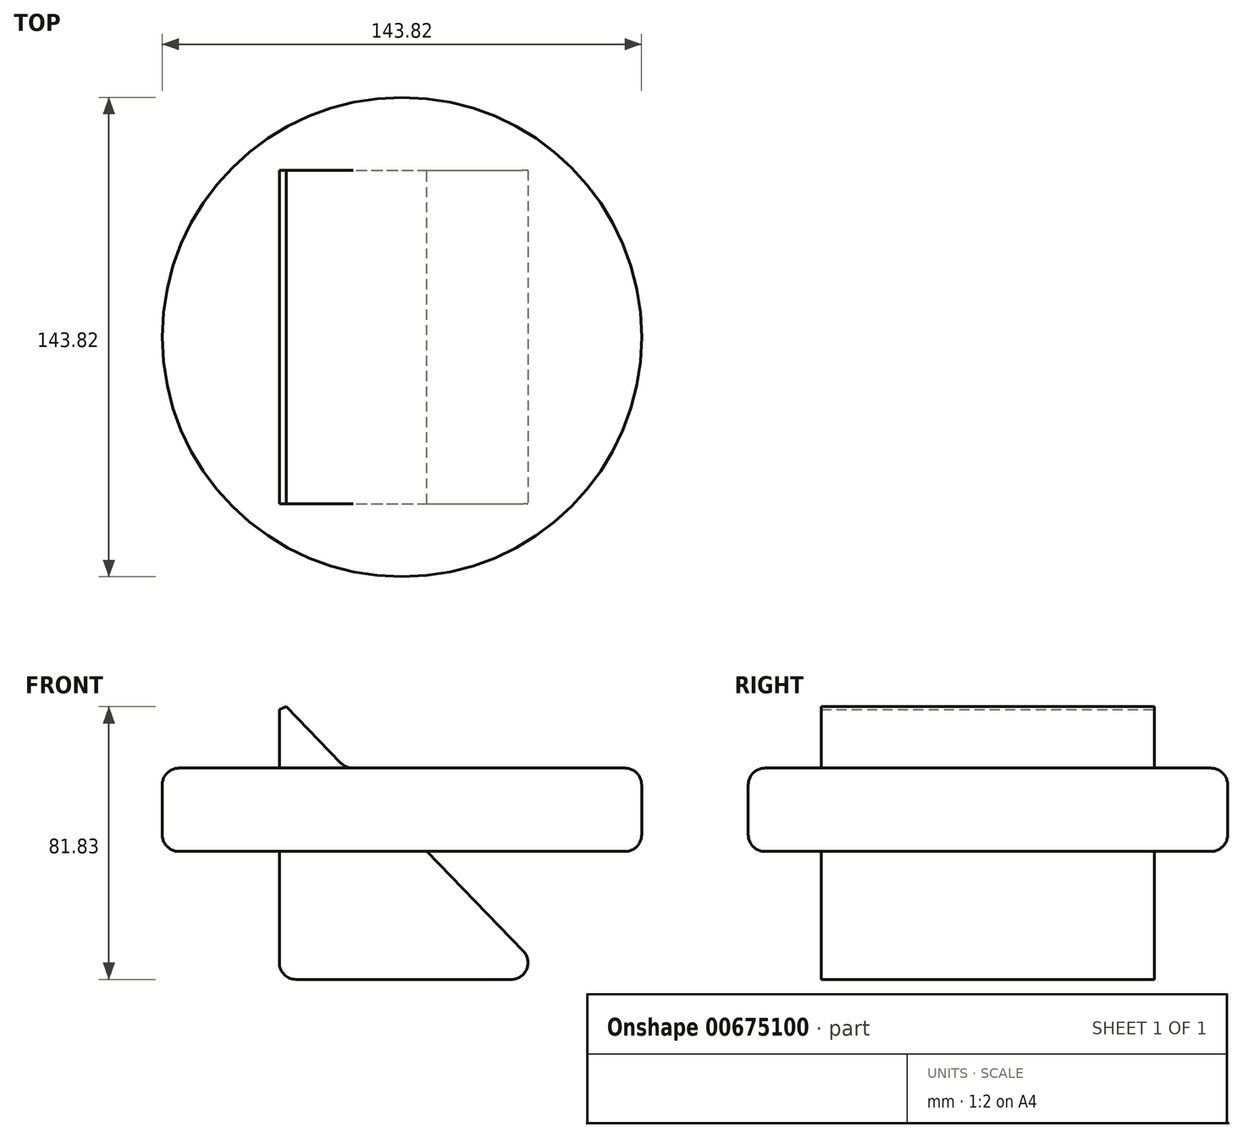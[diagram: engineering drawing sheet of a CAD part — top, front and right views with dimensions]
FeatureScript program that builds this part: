
annotation { "Feature Type Name" : "Feature", "Feature Type Description" : "" }
export const myFeature = defineFeature(function(context is Context, id is Id, definition is map)
    precondition{}
    {
        {
            var Q0;
            Q0=qCreatedBy(makeId("Top.planeOp"),FACE);
            var sketch = newSketch(context, id + "F0", { "sketchPlane" : qUnion([Q0])});
            skCircle(sketch, "E0", {"center": v(0, 0) * mm, "radius": 71.91 * mm});
            skSolve(sketch);
        }
        {
            var Q0;
            Q0=makeQuery(id+"F0.imprint","IMPRINT",FACE,{"disambiguationData":[TD([[makeQuery(id+"F0.imprint","IMPRINT",EDGE,{"derivedFrom":sQuery(id+"F0.wireOp",EDGE,"E0")}),1.0]])]});
            extrude(context, id + "F1", {"entities" : qUnion([Q0]), "depth" : 25 * mm, "offsetDistance" : 25 * mm});
        }
        {
            var Q0;
            Q0=qCreatedBy(makeId("Front.planeOp"),FACE);
            var sketch = newSketch(context, id + "F2", { "sketchPlane" : qUnion([Q0])});
            skLineSegment(sketch, "E1", {"start": v(-36.8, 42.55) * mm, "end": v(-36.8, -38.4) * mm});
            skLineSegment(sketch, "E2", {"start": v(-36.8, -38.4) * mm, "end": v(44.6, -38.4) * mm});
            skLineSegment(sketch, "E3", {"start": v(-34.66, 43.44) * mm, "end": v(44.6, -38.4) * mm});
            skLineSegment(sketch, "E4", {"start": v(-34.66, 43.44) * mm, "end": v(-36.8, 42.55) * mm});
            skSolve(sketch);
        }
        {
            var Q0;
            Q0 = qSketchRegion(id + "F2", true);
            extrude(context, id + "F3", {"entities" : qUnion([Q0]), "operationType" : NewBodyOperationType.ADD, "endBound" : BoundingType.SYMMETRIC, "depth" : 100 * mm, "offsetDistance" : 25 * mm});
        }
        {
            var Q0;
            Q0=makeQuery(id+"F3.opExtrude","SWEPT_EDGE",EDGE,{"disambiguationData":[OSD([sQuery(id+"F2.wireOp",EDGE,"E2"),sQuery(id+"F2.wireOp",EDGE,"E3")])]});
            fillet(context, id + "F4", {"entities" : qUnion([Q0]), "radius" : 5 * mm, "tangentPropagation" : true, "allowEdgeOverflow" : false});
        }
        {
            var Q0;
            Q0=makeQuery(id+"F3.opExtrude","SWEPT_EDGE",EDGE,{"disambiguationData":[OSD([sQuery(id+"F2.wireOp",EDGE,"E1"),sQuery(id+"F2.wireOp",EDGE,"E2")])]});
            fillet(context, id + "F5", {"entities" : qUnion([Q0]), "radius" : 5 * mm, "tangentPropagation" : true, "allowEdgeOverflow" : false});
        }
        {
            var Q0;
            Q0=makeQuery(id+"F1.opExtrude","CAP_EDGE",EDGE,{"disambiguationData":[OSD([sQuery(id+"F0.wireOp",EDGE,"E0")])],"isStart":false});
            fillet(context, id + "F6", {"entities" : qUnion([Q0]), "radius" : 5 * mm, "tangentPropagation" : true, "allowEdgeOverflow" : false});
        }
        {
            var Q0;
            Q0=makeQuery(id+"F1.opExtrude","CAP_EDGE",EDGE,{"disambiguationData":[OSD([sQuery(id+"F0.wireOp",EDGE,"E0")])],"isStart":true});
            fillet(context, id + "F7", {"entities" : qUnion([Q0]), "radius" : 5 * mm, "tangentPropagation" : true, "allowEdgeOverflow" : false});
        }
        {
            var Q0;
            Q0=makeQuery(id+"F3.boolean.opBoolean","INTERSECT",EDGE,{"derivedFrom":[makeQuery(id+"F1.opExtrude","CAP_FACE",FACE,{"disambiguationData":[OSD([sQuery(id+"F0.wireOp",EDGE,"E0")])],"isStart":false}),makeQuery(id+"F3.opExtrude","SWEPT_FACE",FACE,{"disambiguationData":[OSD([sQuery(id+"F2.wireOp",EDGE,"E3")])]})]});
            fillet(context, id + "F8", {"entities" : qUnion([Q0]), "radius" : 5 * mm, "tangentPropagation" : true, "allowEdgeOverflow" : false});
        }
    });
